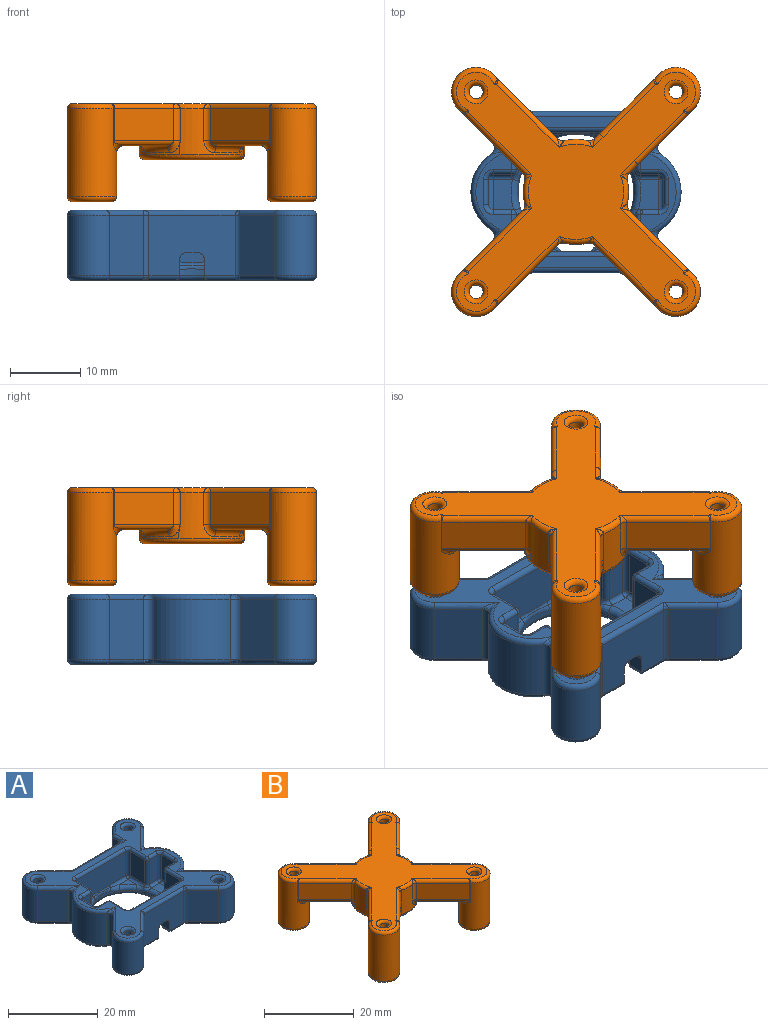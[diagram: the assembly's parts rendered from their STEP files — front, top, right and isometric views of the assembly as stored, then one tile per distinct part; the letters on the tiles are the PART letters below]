
ASSEMBLY  parts=2 mates=1
PART A: 206 faces, bbox 36.7x36.7x10.6 mm
  f0: plane 2.83x2.83mm, normal (0,0,1), area 3.4mm2, adj f98,f108,f177
  f1: plane 4.38x2.92mm, normal (0,0,1), area 11.4mm2, adj f36,f87,f107,f111,f112,f171
  f2: plane 4.15x3.53mm, normal (0,0,1), area 5.8mm2, adj f39,f63,f162
  f3: plane 4.38x2.92mm, normal (0,0,1), area 11.4mm2, adj f40,f57,f65,f75,f80,f168
  f4: plane 4.15x3.53mm, normal (0,0,1), area 5.8mm2, adj f37,f74,f165
  f5: plane 14.64x8.6mm, normal (0,1,0), area 125.9mm2, adj f113,f156,f198,f204
  f6: plane 8.6x4.93mm, normal (0.71,0.71,0), area 60mm2, adj f7,f114,f157,f204
  f7: cylinder r=3.5mm len=8.6mm, axis (0,0,1), area 94.6mm2, adj f6,f8,f116,f155
  f8: plane 8.6x4.81mm, normal (-0.71,-0.71,0), area 58.5mm2, adj f7,f118,f153,f183
  f9: cylinder r=6.5mm len=10.85mm, axis (0,0,1), area 110.3mm2, adj f120,f151,f183,f189
  f10: plane 8.6x4.81mm, normal (-0.71,0.71,0), area 58.5mm2, adj f11,f122,f149,f189
  f11: cylinder r=3.5mm len=8.6mm, axis (0,0,1), area 94.6mm2, adj f10,f12,f124,f147
  f12: plane 8.6x4.93mm, normal (0.71,-0.71,0), area 60mm2, adj f11,f126,f145,f192
  f13: plane 12.27x8.6mm, normal (0,-1,0), area 94.4mm2, adj f14,f16,f44,f128,f131,f143,f180,f181
  f14: plane 2.49x2.3mm, normal (1,0,0), area 5.7mm2, adj f13,f54,f130,f180
  f15: cylinder r=8.25mm len=16.5mm, axis (0,0,1), area 18.9mm2, adj f53,f54,f134,f161,f162,f163,f164,f165
  f16: plane 2.49x2.3mm, normal (-1,0,0), area 5.7mm2, adj f13,f53,f133,f181
  f17: plane 8.6x4.93mm, normal (-0.71,-0.71,0), area 60mm2, adj f18,f129,f141,f195
  f18: cylinder r=3.5mm len=8.6mm, axis (0,0,1), area 94.6mm2, adj f17,f19,f127,f142
  f19: plane 8.6x4.81mm, normal (0.71,0.71,0), area 58.5mm2, adj f18,f125,f144,f186
  f20: cylinder r=6.5mm len=10.85mm, axis (0,0,1), area 110.3mm2, adj f123,f146,f186,f201
  f21: plane 8.6x4.81mm, normal (0.71,-0.71,0), area 58.5mm2, adj f22,f121,f148,f201
  f22: cylinder r=3.5mm len=8.6mm, axis (0,0,1), area 94.6mm2, adj f21,f23,f119,f150
  f23: plane 8.6x2.28mm, normal (-0.71,0.71,0), area 27.7mm2, adj f22,f27,f117,f152
  f24: cylinder r=1mm len=4.8mm, axis (0,0,1), area 30.2mm2, adj f52,f140
  f25: cylinder r=1mm len=4.8mm, axis (0,0,1), area 30.2mm2, adj f48,f160
  f26: cylinder r=1mm len=4.8mm, axis (0,0,1), area 30.2mm2, adj f50,f158
  f27: plane 8.6x1.95mm, normal (-1,0,0), area 16.8mm2, adj f23,f115,f154,f198
  f28: cylinder r=1mm len=4.8mm, axis (0,0,1), area 30.2mm2, adj f46,f159
  f29: plane 34.1x34.1mm, normal (0,0,-1), area 347.6mm2, adj f113,f114,f115,f116,f117,f118,f119,f120
  f30: plane 2.83x2.83mm, normal (0,0,1), area 3.4mm2, adj f83,f91,f174
  f31: plane 6.6x4.6mm, normal (1,0,0), area 30.4mm2, adj f76,f83,f84,f85
  f32: plane 15.6x6.76mm, normal (0,-1,0), area 103.4mm2, adj f84,f91,f92,f94,f98,f99
  f33: plane 6.6x4.6mm, normal (-1,0,0), area 30.4mm2, adj f99,f100,f108,f109
  f34: plane 6.6x2.6mm, normal (0,-1,0), area 17.2mm2, adj f101,f106,f109,f112
  f35: plane 6.6x3.6mm, normal (-1,0,0), area 23.8mm2, adj f96,f103,f106,f107
  f36: plane 7.3x2.6mm, normal (0,1,0), area 19mm2, adj f1,f87,f93,f103
  f37: plane 7.3x4.6mm, normal (-1,0,0), area 33.6mm2, adj f4,f79,f86,f87,f167
  f38: plane 15.6x6.6mm, normal (0,1,0), area 93.1mm2, adj f55,f59,f63,f64,f69,f74,f78,f79
  f39: plane 7.3x4.6mm, normal (1,0,0), area 33.6mm2, adj f2,f57,f68,f69,f164
  f40: plane 7.3x2.6mm, normal (0,1,0), area 19mm2, adj f3,f56,f57,f60
  f41: plane 6.6x3.6mm, normal (1,0,0), area 23.8mm2, adj f60,f65,f66,f67
  f42: plane 6.6x2.6mm, normal (0,-1,0), area 17.2mm2, adj f66,f75,f76,f77
  f43: plane 34.1x34.1mm, normal (0,0,1), area 278.1mm2, adj f56,f61,f67,f68,f72,f73,f77,f78
  f44: plane 3.22x2.3mm, normal (0,0,-1), area 4.5mm2, adj f13,f53,f54,f59,f180,f181
  f45: cylinder r=2mm len=4mm, axis (0,0,1), area 47.8mm2, adj f46,f139
  f46: plane 4x4mm, normal (0,0,-1), area 9.4mm2, adj f28,f45
  f47: cylinder r=2mm len=4mm, axis (0,0,1), area 47.8mm2, adj f48,f138
  f48: plane 4x4mm, normal (0,0,-1), area 9.4mm2, adj f25,f47
  f49: cylinder r=2mm len=4mm, axis (0,0,1), area 47.8mm2, adj f50,f137
  f50: plane 4x4mm, normal (0,0,-1), area 9.4mm2, adj f26,f49
  f51: cylinder r=2mm len=4mm, axis (0,0,1), area 47.8mm2, adj f52,f136
  f52: plane 4x4mm, normal (0,0,-1), area 9.4mm2, adj f24,f51
  f53: plane 4.02x3.15mm, normal (-0.81,0.59,0), area 2.5mm2, adj f15,f16,f44,f59,f64,f70,f135,f163
  f54: plane 4.02x3.15mm, normal (0.81,0.59,0), area 2.5mm2, adj f14,f15,f44,f55,f58,f59,f132,f161
  f55: cylinder r=0.7mm len=2mm, axis (0,0,-1), area 1.1mm2, adj f38,f54,f58,f59
  f56: cylinder r=0.7mm len=2.6mm, axis (1,0,0), area 2.9mm2, adj f40,f43,f61,f62
  f57: cylinder r=0.7mm len=7.3mm, axis (0,0,-1), area 8mm2, adj f3,f39,f40,f62,f166
  f58: bspline ~1.33x1.26mm, area 1mm2, adj f54,f55,f63,f161
  f59: cylinder r=0.7mm len=4.95mm, axis (-1,0,0), area 4.4mm2, adj f38,f44,f53,f54,f55,f64
  f60: cylinder r=0.7mm len=7.3mm, axis (0,0,1), area 7.6mm2, adj f40,f41,f61,f65
  f61: torus R=1.4mm, axis (0,0,1), area 1.6mm2, adj f43,f56,f60,f67
  f62: sphere r=0.7mm, area 0.5mm2, adj f56,f57,f68
  f63: cylinder r=0.7mm len=6.03mm, axis (-1,0,0), area 5.5mm2, adj f2,f38,f58,f69,f161
  f64: cylinder r=0.7mm len=2mm, axis (0,0,1), area 1.1mm2, adj f38,f53,f59,f70
  f65: cylinder r=0.7mm len=4.3mm, axis (0,1,0), area 4.3mm2, adj f3,f41,f60,f71
  f66: cylinder r=0.7mm len=6.6mm, axis (0,0,-1), area 7.3mm2, adj f41,f42,f71,f72
  f67: cylinder r=0.7mm len=3.6mm, axis (0,-1,0), area 4mm2, adj f41,f43,f61,f72
  f68: cylinder r=0.7mm len=4.6mm, axis (0,-1,0), area 5.1mm2, adj f39,f43,f62,f73
  f69: cylinder r=0.7mm len=7.3mm, axis (0,0,-1), area 7.6mm2, adj f38,f39,f63,f73
  f70: bspline ~1.33x1.26mm, area 1mm2, adj f53,f64,f74,f163
  f71: sphere r=0.7mm, area 0.8mm2, adj f65,f66,f75
  f72: torus R=1.4mm, axis (0,0,1), area 1.6mm2, adj f43,f66,f67,f77
  f73: torus R=1.4mm, axis (0,0,1), area 1.6mm2, adj f43,f68,f69,f78
  f74: cylinder r=0.7mm len=6.03mm, axis (-1,0,0), area 5.5mm2, adj f4,f38,f70,f79,f163
  f75: cylinder r=0.7mm len=2.6mm, axis (1,0,0), area 2.9mm2, adj f3,f42,f71,f80
  f76: cylinder r=0.7mm len=6.6mm, axis (0,0,1), area 7.3mm2, adj f31,f42,f80,f81
  f77: cylinder r=0.7mm len=2.6mm, axis (-1,0,0), area 2.9mm2, adj f42,f43,f72,f81
  f78: cylinder r=0.7mm len=15.6mm, axis (1,0,0), area 17.2mm2, adj f38,f43,f73,f82
  f79: cylinder r=0.7mm len=7.3mm, axis (0,0,1), area 7.6mm2, adj f37,f38,f74,f82
  f80: torus R=1.4mm, axis (0,0,1), area 1.1mm2, adj f3,f75,f76,f83,f170
  f81: sphere r=0.7mm, area 0.8mm2, adj f76,f77,f85
  f82: torus R=1.4mm, axis (0,0,1), area 1.6mm2, adj f43,f78,f79,f86
  f83: cylinder r=0.7mm len=4.6mm, axis (0,1,0), area 4.7mm2, adj f30,f31,f80,f88,f172
  f84: cylinder r=0.7mm len=6.6mm, axis (0,0,1), area 7.3mm2, adj f31,f32,f88,f89
  f85: cylinder r=0.7mm len=4.6mm, axis (0,-1,0), area 5.1mm2, adj f31,f43,f81,f89
  f86: cylinder r=0.7mm len=4.6mm, axis (0,1,0), area 5.1mm2, adj f37,f43,f82,f90
  f87: cylinder r=0.7mm len=7.3mm, axis (0,0,-1), area 8mm2, adj f1,f36,f37,f90,f169
  f88: sphere r=0.7mm, area 1mm2, adj f83,f84,f91
  f89: torus R=1.4mm, axis (0,0,1), area 1.6mm2, adj f43,f84,f85,f92
  f90: sphere r=0.7mm, area 1mm2, adj f86,f87,f93
  f91: cylinder r=0.7mm len=5.11mm, axis (1,0,0), area 5.1mm2, adj f30,f32,f88,f94,f176
  f92: cylinder r=0.7mm len=15.6mm, axis (-1,0,0), area 17.2mm2, adj f32,f43,f89,f95
  f93: cylinder r=0.7mm len=2.6mm, axis (1,0,0), area 2.9mm2, adj f36,f43,f90,f97
  f94: bspline ~6.05x0.89mm, area 2.4mm2, adj f32,f91,f98,f178
  f95: torus R=1.4mm, axis (0,0,1), area 1.6mm2, adj f43,f92,f99,f100
  f96: cylinder r=0.7mm len=3.6mm, axis (0,1,0), area 4mm2, adj f35,f43,f97,f102
  f97: torus R=1.4mm, axis (0,0,1), area 1.6mm2, adj f43,f93,f96,f103
  f98: cylinder r=0.7mm len=5.11mm, axis (1,0,0), area 5.1mm2, adj f0,f32,f94,f104,f179
  f99: cylinder r=0.7mm len=6.6mm, axis (0,0,-1), area 7.3mm2, adj f32,f33,f95,f104
  f100: cylinder r=0.7mm len=4.6mm, axis (0,1,0), area 5.1mm2, adj f33,f43,f95,f105
  f101: cylinder r=0.7mm len=2.6mm, axis (-1,0,0), area 2.9mm2, adj f34,f43,f102,f105
  f102: torus R=1.4mm, axis (0,0,1), area 1.6mm2, adj f43,f96,f101,f106
  f103: cylinder r=0.7mm len=7.3mm, axis (0,0,1), area 7.6mm2, adj f35,f36,f97,f107
  f104: sphere r=0.7mm, area 0.5mm2, adj f98,f99,f108
  f105: sphere r=0.7mm, area 0.8mm2, adj f100,f101,f109
  f106: cylinder r=0.7mm len=6.6mm, axis (0,0,-1), area 7.3mm2, adj f34,f35,f102,f110
  f107: cylinder r=0.7mm len=4.3mm, axis (0,-1,0), area 4.3mm2, adj f1,f35,f103,f110
  f108: cylinder r=0.7mm len=4.6mm, axis (0,-1,0), area 4.7mm2, adj f0,f33,f104,f111,f175
  f109: cylinder r=0.7mm len=6.6mm, axis (0,0,1), area 7.3mm2, adj f33,f34,f105,f111
  f110: sphere r=0.7mm, area 0.5mm2, adj f106,f107,f112
  f111: torus R=1.4mm, axis (0,0,1), area 1.1mm2, adj f1,f108,f109,f112,f173
  f112: cylinder r=0.7mm len=2.6mm, axis (1,0,0), area 2.9mm2, adj f1,f34,f110,f111
  f113: cylinder r=0.7mm len=17.04mm, axis (1,0,0), area 17.4mm2, adj f5,f29,f199,f205
  f114: cylinder r=0.7mm len=5.93mm, axis (0.71,-0.71,0), area 8.1mm2, adj f6,f29,f116,f205
  f115: cylinder r=0.7mm len=3.65mm, axis (0,1,0), area 2.9mm2, adj f27,f29,f117,f199
  f116: torus R=2.8mm, axis (0,0,1), area 11.2mm2, adj f7,f29,f114,f118
  f117: cylinder r=0.7mm len=2.77mm, axis (0.71,0.71,0), area 3.4mm2, adj f23,f29,f115,f119
  f118: cylinder r=0.7mm len=7.08mm, axis (-0.71,0.71,0), area 8.9mm2, adj f8,f29,f116,f184
  f119: torus R=2.8mm, axis (0,0,1), area 11.2mm2, adj f22,f29,f117,f121
  f120: torus R=5.8mm, axis (0,0,1), area 16.1mm2, adj f9,f29,f184,f190
  f121: cylinder r=0.7mm len=7.08mm, axis (-0.71,-0.71,0), area 8.9mm2, adj f21,f29,f119,f202
  f122: cylinder r=0.7mm len=7.08mm, axis (0.71,0.71,0), area 8.9mm2, adj f10,f29,f124,f190
  f123: torus R=5.8mm, axis (0,0,1), area 16.1mm2, adj f20,f29,f187,f202
  f124: torus R=2.8mm, axis (0,0,1), area 11.2mm2, adj f11,f29,f122,f126
  f125: cylinder r=0.7mm len=7.08mm, axis (0.71,-0.71,0), area 8.9mm2, adj f19,f29,f127,f187
  f126: cylinder r=0.7mm len=5.93mm, axis (-0.71,-0.71,0), area 8.1mm2, adj f12,f29,f124,f193
  f127: torus R=2.8mm, axis (0,0,1), area 11.2mm2, adj f18,f29,f125,f129
  f128: cylinder r=0.7mm len=5.09mm, axis (-1,0,0), area 4.8mm2, adj f13,f29,f130,f193
  f129: cylinder r=0.7mm len=5.93mm, axis (-0.71,0.71,0), area 8.1mm2, adj f17,f29,f127,f196
  f130: cylinder r=0.7mm len=2.49mm, axis (0,-1,0), area 2.2mm2, adj f14,f29,f128,f132
  f131: cylinder r=0.7mm len=5.09mm, axis (-1,0,0), area 4.8mm2, adj f13,f29,f133,f196
  f132: cylinder r=0.7mm len=1.59mm, axis (0.59,-0.81,0), area 1.4mm2, adj f29,f54,f130,f134
  f133: cylinder r=0.7mm len=2.49mm, axis (0,1,0), area 2.2mm2, adj f16,f29,f131,f135
  f134: torus R=8.95mm, axis (0,0,1), area 52.5mm2, adj f15,f29,f132,f135
  f135: cylinder r=0.7mm len=1.59mm, axis (0.59,0.81,0), area 1.4mm2, adj f29,f53,f133,f134
  f136: torus R=2.7mm, axis (0,0,1), area 15.6mm2, adj f29,f51
  f137: torus R=2.7mm, axis (0,0,1), area 15.6mm2, adj f29,f49
  f138: torus R=2.7mm, axis (0,0,1), area 15.6mm2, adj f29,f47
  f139: torus R=2.7mm, axis (0,0,1), area 15.6mm2, adj f29,f45
  f140: torus R=1.7mm, axis (0,0,1), area 8.7mm2, adj f24,f43
  f141: cylinder r=0.7mm len=5.93mm, axis (0.71,-0.71,0), area 8.1mm2, adj f17,f43,f142,f194
  f142: torus R=2.8mm, axis (0,0,1), area 11.2mm2, adj f18,f43,f141,f144
  f143: cylinder r=0.7mm len=13.68mm, axis (1,0,0), area 14.3mm2, adj f13,f43,f191,f194
  f144: cylinder r=0.7mm len=7.08mm, axis (-0.71,0.71,0), area 8.9mm2, adj f19,f43,f142,f185
  f145: cylinder r=0.7mm len=5.93mm, axis (0.71,0.71,0), area 8.1mm2, adj f12,f43,f147,f191
  f146: torus R=5.8mm, axis (0,0,1), area 16.1mm2, adj f20,f43,f185,f200
  f147: torus R=2.8mm, axis (0,0,1), area 11.2mm2, adj f11,f43,f145,f149
  f148: cylinder r=0.7mm len=7.08mm, axis (0.71,0.71,0), area 8.9mm2, adj f21,f43,f150,f200
  f149: cylinder r=0.7mm len=7.08mm, axis (-0.71,-0.71,0), area 8.9mm2, adj f10,f43,f147,f188
  f150: torus R=2.8mm, axis (0,0,1), area 11.2mm2, adj f22,f43,f148,f152
  f151: torus R=5.8mm, axis (0,0,1), area 16.1mm2, adj f9,f43,f182,f188
  f152: cylinder r=0.7mm len=2.77mm, axis (-0.71,-0.71,0), area 3.4mm2, adj f23,f43,f150,f154
  f153: cylinder r=0.7mm len=7.08mm, axis (0.71,-0.71,0), area 8.9mm2, adj f8,f43,f155,f182
  f154: cylinder r=0.7mm len=3.65mm, axis (0,-1,0), area 2.9mm2, adj f27,f43,f152,f197
  f155: torus R=2.8mm, axis (0,0,1), area 11.2mm2, adj f7,f43,f153,f157
  f156: cylinder r=0.7mm len=17.04mm, axis (-1,0,0), area 17.4mm2, adj f5,f43,f197,f203
  f157: cylinder r=0.7mm len=5.93mm, axis (-0.71,0.71,0), area 8.1mm2, adj f6,f43,f155,f203
  f158: torus R=1.7mm, axis (0,0,1), area 8.7mm2, adj f26,f43
  f159: torus R=1.7mm, axis (0,0,1), area 8.7mm2, adj f28,f43
  f160: torus R=1.7mm, axis (0,0,1), area 8.7mm2, adj f25,f43
  f161: bspline ~3.8x1.78mm, area 2.6mm2, adj f15,f54,f58,f63,f162
  f162: torus R=9.25mm, axis (0,0,1), area 8.1mm2, adj f2,f15,f161,f164
  f163: bspline ~3.8x1.78mm, area 2.6mm2, adj f15,f53,f70,f74,f165
  f164: bspline ~1.16x1.04mm, area 0.6mm2, adj f15,f39,f162,f166
  f165: torus R=9.25mm, axis (0,0,1), area 8.1mm2, adj f4,f15,f163,f167
  f166: bspline ~1.26x1.11mm, area 0.9mm2, adj f15,f57,f164,f168
  f167: bspline ~1.39x1.12mm, area 0.6mm2, adj f15,f37,f165,f169
  f168: torus R=9.25mm, axis (0,0,1), area 6.5mm2, adj f3,f15,f166,f170
  f169: bspline ~1.27x1.13mm, area 0.9mm2, adj f15,f87,f167,f171
  f170: bspline ~1.83x1.44mm, area 1.7mm2, adj f15,f80,f168,f172
  f171: torus R=9.25mm, axis (0,0,1), area 6.5mm2, adj f1,f15,f169,f173
  f172: bspline ~3.03x1.41mm, area 2.3mm2, adj f15,f83,f170,f174
  f173: bspline ~1.83x1.44mm, area 1.7mm2, adj f15,f111,f171,f175
  f174: torus R=9.25mm, axis (0,0,1), area 5.9mm2, adj f15,f30,f172,f176
  f175: bspline ~3.25x1.55mm, area 2.3mm2, adj f15,f108,f173,f177
  f176: bspline ~3.62x1.59mm, area 2.8mm2, adj f15,f91,f174,f178
  f177: torus R=9.25mm, axis (0,0,1), area 5.9mm2, adj f0,f15,f175,f179
  f178: bspline ~5.89x0.92mm, area 3.5mm2, adj f15,f94,f176,f179
  f179: bspline ~3.4x1.45mm, area 2.8mm2, adj f15,f98,f177,f178
  f180: cylinder r=1mm len=2.49mm, axis (0,1,0), area 2.8mm2, adj f13,f14,f44,f54
  f181: cylinder r=1mm len=2.49mm, axis (0,-1,0), area 2.8mm2, adj f13,f16,f44,f53
  f182: bspline ~2.43x1.54mm, area 1.1mm2, adj f151,f153,f183
  f183: cylinder r=1mm len=8.6mm, axis (0,0,1), area 15.2mm2, adj f8,f9,f182,f184
  f184: bspline ~2.43x1.54mm, area 1.1mm2, adj f118,f120,f183
  f185: bspline ~2.43x1.54mm, area 1.1mm2, adj f144,f146,f186
  f186: cylinder r=1mm len=8.6mm, axis (0,0,1), area 15.2mm2, adj f19,f20,f185,f187
  f187: bspline ~2.43x1.54mm, area 1.1mm2, adj f123,f125,f186
  f188: bspline ~2.43x1.54mm, area 1.1mm2, adj f149,f151,f189
  f189: cylinder r=1mm len=8.6mm, axis (0,0,1), area 15.2mm2, adj f9,f10,f188,f190
  f190: bspline ~2.43x1.54mm, area 1.1mm2, adj f120,f122,f189
  f191: bspline ~0.99x0.72mm, area 0.4mm2, adj f143,f145,f192
  f192: cylinder r=1mm len=8.6mm, axis (0,0,1), area 6.8mm2, adj f12,f13,f191,f193
  f193: bspline ~0.99x0.72mm, area 0.4mm2, adj f126,f128,f192
  f194: bspline ~0.99x0.72mm, area 0.4mm2, adj f141,f143,f195
  f195: cylinder r=1mm len=8.6mm, axis (0,0,-1), area 6.8mm2, adj f13,f17,f194,f196
  f196: bspline ~0.99x0.79mm, area 0.4mm2, adj f129,f131,f195
  f197: bspline ~1.7x1.7mm, area 0.7mm2, adj f154,f156,f198
  f198: cylinder r=1mm len=8.6mm, axis (0,0,-1), area 13.5mm2, adj f5,f27,f197,f199
  f199: bspline ~1.7x1.7mm, area 0.7mm2, adj f113,f115,f198
  f200: bspline ~2.43x1.54mm, area 1.1mm2, adj f146,f148,f201
  f201: cylinder r=1mm len=8.6mm, axis (0,0,1), area 15.2mm2, adj f20,f21,f200,f202
  f202: bspline ~2.43x1.54mm, area 1.1mm2, adj f121,f123,f201
  f203: bspline ~0.99x0.79mm, area 0.4mm2, adj f156,f157,f204
  f204: cylinder r=1mm len=8.6mm, axis (0,0,1), area 6.8mm2, adj f5,f6,f203,f205
  f205: bspline ~0.99x0.72mm, area 0.4mm2, adj f113,f114,f204
PART B: 130 faces, bbox 36.1x36.1x14.1 mm
  f0: plane 10.04x10.04mm, normal (0,0,-1), area 42.7mm2, adj f55,f56,f57,f58,f114,f119
  f1: plane 10.04x10.04mm, normal (0,0,-1), area 42.7mm2, adj f50,f59,f93,f125
  f2: plane 10.04x10.04mm, normal (0,0,-1), area 42.7mm2, adj f53,f54,f100,f128
  f3: cylinder r=3.5mm len=12.6mm, axis (0,0,-1), area 221.6mm2, adj f4,f28,f44,f82,f124,f125,f126
  f4: plane 5.37x0.23mm, normal (-1,0,0), area 0.8mm2, adj f3,f5,f59,f80,f126
  f5: plane 8.43x8.43mm, normal (-0.71,-0.71,0), area 54.8mm2, adj f4,f59,f78,f91
  f6: plane 8.43x8.43mm, normal (-0.71,0.71,0), area 54.8mm2, adj f7,f54,f74,f102
  f7: plane 5.37x0.23mm, normal (-1,0,0), area 0.8mm2, adj f6,f8,f54,f72,f127
  f8: cylinder r=3.5mm len=12.6mm, axis (0,0,-1), area 221.6mm2, adj f7,f9,f42,f70,f127,f128,f129
  f9: plane 5.37x0.23mm, normal (0,-1,0), area 0.8mm2, adj f8,f10,f53,f68,f129
  f10: plane 8.43x8.43mm, normal (0.71,-0.71,0), area 54.8mm2, adj f9,f53,f66,f98
  f11: plane 8.43x8.43mm, normal (-0.71,-0.71,0), area 54.8mm2, adj f12,f51,f62,f109
  f12: plane 5.37x0.23mm, normal (0,-1,0), area 0.8mm2, adj f11,f13,f51,f61,f121
  f13: cylinder r=3.5mm len=12.6mm, axis (0,0,-1), area 221.6mm2, adj f12,f14,f46,f63,f121,f122,f123
  f14: plane 5.37x0.23mm, normal (1,0,0), area 0.8mm2, adj f13,f15,f52,f65,f123
  f15: plane 8.43x8.43mm, normal (0.71,0.71,0), area 54.8mm2, adj f14,f52,f67,f105
  f16: plane 4.6x1.29mm, normal (0.71,-0.71,0), area 8.4mm2, adj f17,f55,f71,f116
  f17: plane 7.14x7.14mm, normal (0.71,-0.71,0), area 46.4mm2, adj f16,f18,f56,f73
  f18: plane 5.37x0.23mm, normal (1,0,0), area 0.8mm2, adj f17,f19,f56,f75,f118
  f19: cylinder r=3.5mm len=12.6mm, axis (0,0,-1), area 221.6mm2, adj f18,f20,f49,f77,f118,f119,f120
  f20: plane 5.37x0.23mm, normal (0,1,0), area 0.8mm2, adj f19,f21,f57,f79,f120
  f21: plane 7.69x7.69mm, normal (-0.71,0.71,0), area 50mm2, adj f20,f22,f57,f81
  f22: plane 4.6x0.74mm, normal (-0.71,0.71,0), area 4.8mm2, adj f21,f58,f83,f112
  f23: cylinder r=7.5mm len=15mm, axis (0,0,-1), area 111.5mm2, adj f40,f64,f69,f76,f85,f91,f92,f93
  f24: plane 8.43x8.43mm, normal (0.71,0.71,0), area 54.8mm2, adj f28,f50,f86,f95
  f25: cylinder r=1mm len=12.6mm, axis (0,0,-1), area 79.2mm2, adj f43,f88
  f26: cylinder r=1mm len=12.6mm, axis (0,0,-1), area 79.2mm2, adj f48,f89
  f27: cylinder r=1mm len=12.6mm, axis (0,0,-1), area 79.2mm2, adj f45,f60
  f28: plane 5.37x0.23mm, normal (0,1,0), area 0.8mm2, adj f3,f24,f50,f84,f124
  f29: cylinder r=1mm len=12.6mm, axis (0,0,-1), area 79.2mm2, adj f47,f87
  f30: plane 34.1x34.1mm, normal (0,0,1), area 460.9mm2, adj f60,f61,f62,f63,f64,f65,f66,f67
  f31: plane 10.04x10.04mm, normal (0,0,-1), area 42.7mm2, adj f51,f52,f107,f122
  f32: plane 5.6x5.6mm, normal (0,0,-1), area 15.6mm2, adj f44,f45
  f33: plane 5.6x5.6mm, normal (0,0,-1), area 15.6mm2, adj f48,f49
  f34: plane 5.6x5.6mm, normal (0,0,-1), area 15.6mm2, adj f46,f47
  f35: plane 5.6x5.6mm, normal (0,0,-1), area 15.6mm2, adj f42,f43
  f36: cylinder r=5mm len=10mm, axis (0,0,1), area 18.8mm2, adj f39,f41
  f37: plane 13.6x13.6mm, normal (0,0,-1), area 43.2mm2, adj f40,f41
  f38: plane 8.6x8.6mm, normal (0,0,-1), area 58.1mm2, adj f39
  f39: torus R=4.3mm, axis (0,0,1), area 32.8mm2, adj f36,f38
  f40: torus R=6.8mm, axis (0,0,1), area 50.1mm2, adj f23,f37
  f41: torus R=5.7mm, axis (0,0,1), area 36.3mm2, adj f36,f37
  f42: torus R=2.8mm, axis (0,0,1), area 22.4mm2, adj f8,f35
  f43: torus R=1.7mm, axis (0,0,1), area 8.7mm2, adj f25,f35
  f44: torus R=2.8mm, axis (0,0,1), area 22.4mm2, adj f3,f32
  f45: torus R=1.7mm, axis (0,0,1), area 8.7mm2, adj f27,f32
  f46: torus R=2.8mm, axis (0,0,1), area 22.4mm2, adj f13,f34
  f47: torus R=1.7mm, axis (0,0,1), area 8.7mm2, adj f29,f34
  f48: torus R=1.7mm, axis (0,0,1), area 8.7mm2, adj f26,f33
  f49: torus R=2.8mm, axis (0,0,1), area 22.4mm2, adj f19,f33
  f50: cylinder r=0.7mm len=8.95mm, axis (-0.71,0.71,0), area 11.6mm2, adj f1,f24,f28,f94,f124
  f51: cylinder r=0.7mm len=8.95mm, axis (0.71,-0.71,0), area 11.6mm2, adj f11,f12,f31,f108,f121
  f52: cylinder r=0.7mm len=8.95mm, axis (-0.71,0.71,0), area 11.6mm2, adj f14,f15,f31,f106,f123
  f53: cylinder r=0.7mm len=8.95mm, axis (0.71,0.71,0), area 11.6mm2, adj f2,f9,f10,f99,f129
  f54: cylinder r=0.7mm len=8.95mm, axis (-0.71,-0.71,0), area 11.6mm2, adj f2,f6,f7,f101,f127
  f55: cylinder r=0.7mm len=1.78mm, axis (0.71,0.71,0), area 1.6mm2, adj f0,f16,f56,f115
  f56: cylinder r=0.7mm len=7.67mm, axis (0.71,0.71,0), area 10.1mm2, adj f0,f17,f18,f55,f118
  f57: cylinder r=0.7mm len=8.22mm, axis (-0.71,-0.71,0), area 10.9mm2, adj f0,f20,f21,f58,f120
  f58: cylinder r=0.7mm len=1.23mm, axis (-0.71,-0.71,0), area 0.8mm2, adj f0,f22,f57,f113
  f59: cylinder r=0.7mm len=8.95mm, axis (0.71,-0.71,0), area 11.6mm2, adj f1,f4,f5,f92,f126
  f60: torus R=1.7mm, axis (0,0,1), area 8.7mm2, adj f27,f30
  f61: cylinder r=0.7mm len=0.7mm, axis (-1,0,0), area 0.2mm2, adj f12,f30,f62,f63
  f62: cylinder r=0.7mm len=9.64mm, axis (-0.71,0.71,0), area 13.5mm2, adj f11,f30,f61,f110
  f63: torus R=2.8mm, axis (0,0,1), area 13.6mm2, adj f13,f30,f61,f65
  f64: torus R=6.8mm, axis (0,0,1), area 4.7mm2, adj f23,f30,f97,f110
  f65: cylinder r=0.7mm len=0.7mm, axis (0,-1,0), area 0.2mm2, adj f14,f30,f63,f67
  f66: cylinder r=0.7mm len=9.64mm, axis (-0.71,-0.71,0), area 13.5mm2, adj f10,f30,f68,f97
  f67: cylinder r=0.7mm len=9.64mm, axis (0.71,-0.71,0), area 13.5mm2, adj f15,f30,f65,f104
  f68: cylinder r=0.7mm len=0.7mm, axis (-1,0,0), area 0.2mm2, adj f9,f30,f66,f70
  f69: torus R=6.8mm, axis (0,0,1), area 4.7mm2, adj f23,f30,f104,f117
  f70: torus R=2.8mm, axis (0,0,1), area 13.6mm2, adj f8,f30,f68,f72
  f71: cylinder r=0.7mm len=2.5mm, axis (-0.71,-0.71,0), area 2.6mm2, adj f16,f30,f73,f117
  f72: cylinder r=0.7mm len=0.7mm, axis (0,1,0), area 0.2mm2, adj f7,f30,f70,f74
  f73: cylinder r=0.7mm len=7.63mm, axis (-0.71,-0.71,0), area 10.9mm2, adj f17,f30,f71,f75
  f74: cylinder r=0.7mm len=9.64mm, axis (0.71,0.71,0), area 13.5mm2, adj f6,f30,f72,f103
  f75: cylinder r=0.7mm len=0.7mm, axis (0,-1,0), area 0.2mm2, adj f18,f30,f73,f77
  f76: torus R=6.8mm, axis (0,0,1), area 4.7mm2, adj f23,f30,f90,f103
  f77: torus R=2.8mm, axis (0,0,1), area 13.6mm2, adj f19,f30,f75,f79
  f78: cylinder r=0.7mm len=9.64mm, axis (-0.71,0.71,0), area 13.5mm2, adj f5,f30,f80,f90
  f79: cylinder r=0.7mm len=0.7mm, axis (1,0,0), area 0.2mm2, adj f20,f30,f77,f81
  f80: cylinder r=0.7mm len=0.7mm, axis (0,1,0), area 0.2mm2, adj f4,f30,f78,f82
  f81: cylinder r=0.7mm len=8.19mm, axis (0.71,0.71,0), area 11.8mm2, adj f21,f30,f79,f83
  f82: torus R=2.8mm, axis (0,0,1), area 13.6mm2, adj f3,f30,f80,f84
  f83: cylinder r=0.7mm len=1.95mm, axis (0.71,0.71,0), area 1.7mm2, adj f22,f30,f81,f111
  f84: cylinder r=0.7mm len=0.7mm, axis (1,0,0), area 0.2mm2, adj f28,f30,f82,f86
  f85: torus R=6.8mm, axis (0,0,1), area 4.7mm2, adj f23,f30,f96,f111
  f86: cylinder r=0.7mm len=9.64mm, axis (0.71,-0.71,0), area 13.5mm2, adj f24,f30,f84,f96
  f87: torus R=1.7mm, axis (0,0,1), area 8.7mm2, adj f29,f30
  f88: torus R=1.7mm, axis (0,0,1), area 8.7mm2, adj f25,f30
  f89: torus R=1.7mm, axis (0,0,1), area 8.7mm2, adj f26,f30
  f90: bspline ~1.21x0.93mm, area 0.5mm2, adj f76,f78,f91
  f91: cylinder r=1mm len=4.6mm, axis (0,0,-1), area 4.7mm2, adj f5,f23,f90,f92
  f92: bspline ~2.2x2.04mm, area 2.3mm2, adj f23,f59,f91,f93
  f93: torus R=8.5mm, axis (0,0,1), area 8.3mm2, adj f1,f23,f92,f94
  f94: bspline ~2.2x1.79mm, area 2.3mm2, adj f23,f50,f93,f95
  f95: cylinder r=1mm len=4.6mm, axis (0,0,-1), area 4.7mm2, adj f23,f24,f94,f96
  f96: bspline ~1.21x0.93mm, area 0.5mm2, adj f85,f86,f95
  f97: bspline ~1.21x0.93mm, area 0.5mm2, adj f64,f66,f98
  f98: cylinder r=1mm len=4.6mm, axis (0,0,-1), area 4.7mm2, adj f10,f23,f97,f99
  f99: bspline ~2.2x2.04mm, area 2.3mm2, adj f23,f53,f98,f100
  f100: torus R=8.5mm, axis (0,0,1), area 8.3mm2, adj f2,f23,f99,f101
  f101: bspline ~2.2x1.79mm, area 2.3mm2, adj f23,f54,f100,f102
  f102: cylinder r=1mm len=4.6mm, axis (0,0,-1), area 4.7mm2, adj f6,f23,f101,f103
  f103: bspline ~1.21x0.93mm, area 0.5mm2, adj f74,f76,f102
  f104: bspline ~1.21x0.93mm, area 0.5mm2, adj f67,f69,f105
  f105: cylinder r=1mm len=4.6mm, axis (0,0,-1), area 4.7mm2, adj f15,f23,f104,f106
  f106: bspline ~2.2x2.04mm, area 2.3mm2, adj f23,f52,f105,f107
  f107: torus R=8.5mm, axis (0,0,1), area 8.3mm2, adj f23,f31,f106,f108
  f108: bspline ~2.2x1.79mm, area 2.3mm2, adj f23,f51,f107,f109
  f109: cylinder r=1mm len=4.6mm, axis (0,0,-1), area 4.7mm2, adj f11,f23,f108,f110
  f110: bspline ~1.21x0.93mm, area 0.5mm2, adj f62,f64,f109
  f111: bspline ~1.21x0.93mm, area 0.5mm2, adj f83,f85,f112
  f112: cylinder r=1mm len=4.6mm, axis (0,0,-1), area 4.7mm2, adj f22,f23,f111,f113
  f113: bspline ~2.05x2.04mm, area 2.3mm2, adj f23,f58,f112,f114
  f114: torus R=8.5mm, axis (0,0,1), area 8.3mm2, adj f0,f23,f113,f115
  f115: bspline ~2.2x1.79mm, area 2.3mm2, adj f23,f55,f114,f116
  f116: cylinder r=1mm len=4.6mm, axis (0,0,-1), area 4.7mm2, adj f16,f23,f115,f117
  f117: bspline ~1.21x0.93mm, area 0.5mm2, adj f69,f71,f116
  f118: bspline ~2.74x1.74mm, area 2.4mm2, adj f18,f19,f56,f119
  f119: torus R=4.5mm, axis (0,0,1), area 8.2mm2, adj f0,f19,f118,f120
  f120: bspline ~2.96x1.79mm, area 2.4mm2, adj f19,f20,f57,f119
  f121: bspline ~2.96x1.79mm, area 2.4mm2, adj f12,f13,f51,f122
  f122: torus R=4.5mm, axis (0,0,1), area 8.2mm2, adj f13,f31,f121,f123
  f123: bspline ~2.96x1.79mm, area 2.4mm2, adj f13,f14,f52,f122
  f124: bspline ~2.96x1.79mm, area 2.4mm2, adj f3,f28,f50,f125
  f125: torus R=4.5mm, axis (0,0,1), area 8.2mm2, adj f1,f3,f124,f126
  f126: bspline ~2.96x1.79mm, area 2.4mm2, adj f3,f4,f59,f125
  f127: bspline ~2.96x1.79mm, area 2.4mm2, adj f7,f8,f54,f128
  f128: torus R=4.5mm, axis (0,0,1), area 8.2mm2, adj f2,f8,f127,f129
  f129: bspline ~2.96x1.79mm, area 2.4mm2, adj f8,f9,f53,f128
PLACE A t=(12.33,1.87,19.58)mm
PLACE B t=(12.33,1.87,36.79)mm
MATE slider A.f7 <-> B.f3  axis (0,0,1) through (-1.92,16.12,26.88)mm
